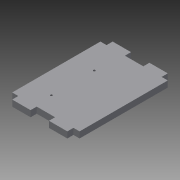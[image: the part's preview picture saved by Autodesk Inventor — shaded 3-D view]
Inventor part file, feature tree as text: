
AUTODESK INVENTOR PART (.ipt)
format: ipt  version: 2014 (Build 180170000, 170)  size: 95,232 bytes
history: native  units: mm
features: reference x4, extrude x1, sketch x1
ambient origin geometry x8: Origin, YZ Plane, XZ Plane, XY Plane, X Axis, Y Axis, Z Axis, Center Point
bodies: 实体1 (feature_tree)
feature tree (6):
  extrude  "拉伸1"  Depth=5.0mm
  sketch  "草图1"  dims[d0=55.0mm d1=5.0mm d2=1.7mm d3=14.0mm d4=37.0mm d5=1.7mm d6=35.0mm d7=18.0mm d8=5.0mm d9=0.0mm]
  reference  "参考1"
  reference  "参考2"
  reference  "参考3"
  reference  "参考4"
